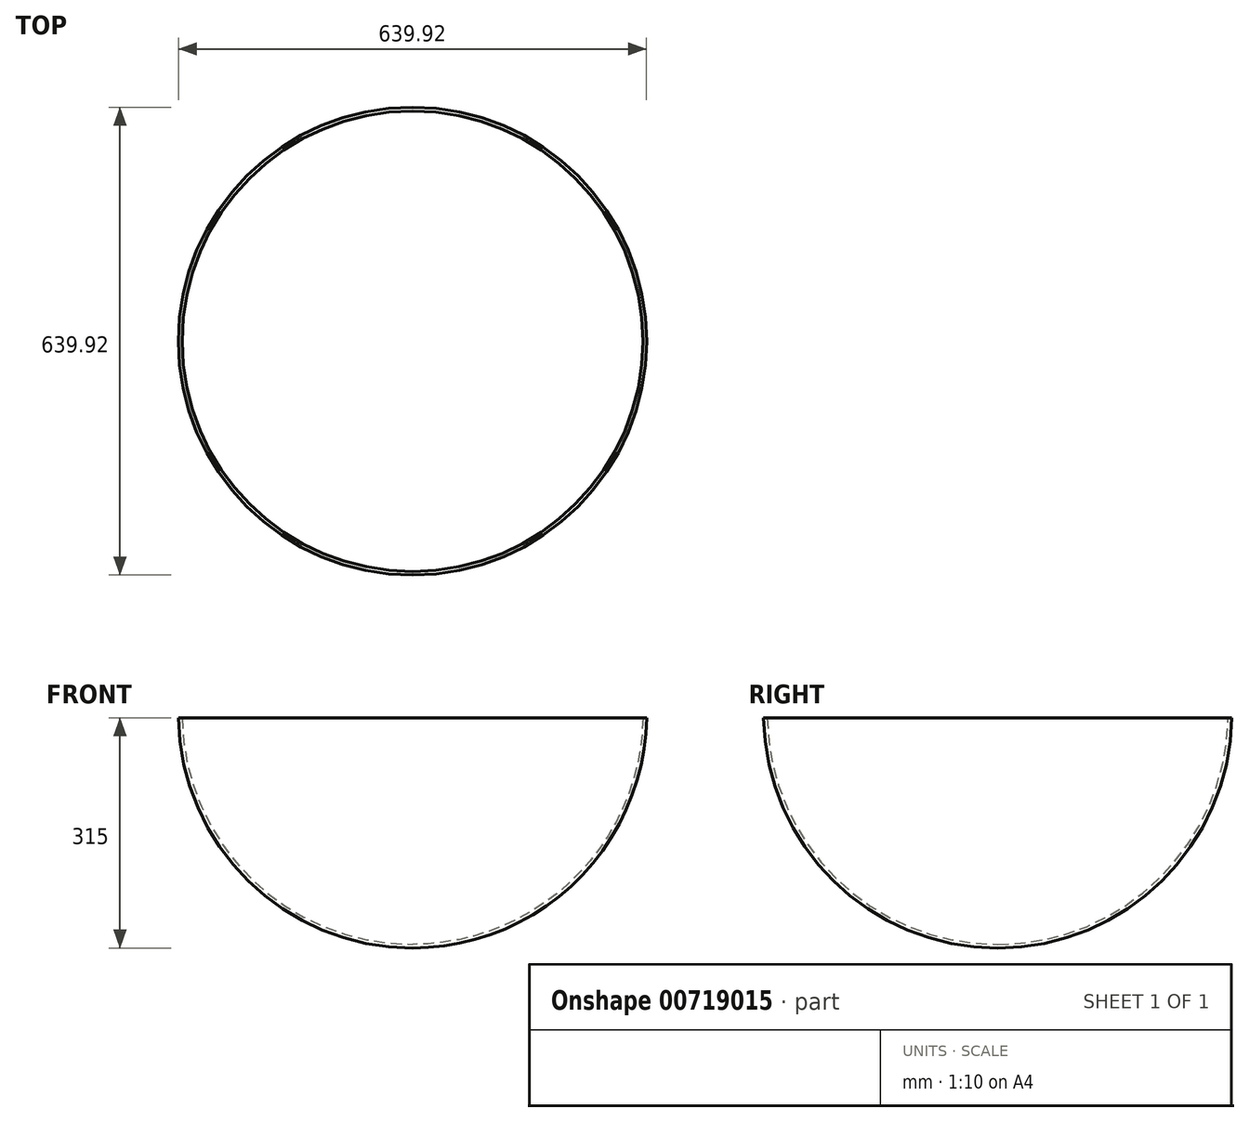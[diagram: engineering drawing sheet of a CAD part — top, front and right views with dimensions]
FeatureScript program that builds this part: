
annotation { "Feature Type Name" : "Feature", "Feature Type Description" : "" }
export const myFeature = defineFeature(function(context is Context, id is Id, definition is map)
    precondition{}
    {
        {
            var Q0;
            Q0=qCreatedBy(makeId("Front.planeOp"),FACE);
            var sketch = newSketch(context, id + "F0", { "sketchPlane" : qUnion([Q0])});
            skArc(sketch, "E0.0", {"start": v(-180.44, -139.56) * mm, "mid": v(44.06, -47.6) * mm, "end": v(139.52, 175.44) * mm});
            skArc(sketch, "E1.0", {"start": v(-180.44, -134.56) * mm, "mid": v(40.53, -44.06) * mm, "end": v(134.52, 175.44) * mm});
            skLineSegment(sketch, "E2", {"start": v(-180.44, -134.56) * mm, "end": v(-180.44, -139.56) * mm});
            skLineSegment(sketch, "E3", {"start": v(134.52, 175.44) * mm, "end": v(139.52, 175.44) * mm});
            skLineSegment(sketch, "E4", {"start": v(-180.44, -134.56) * mm, "end": v(-180.44, 180.44) * mm, "construction": true});
            skLineSegment(sketch, "E5", {"start": v(-180.44, 175.44) * mm, "end": v(189.02, 175.44) * mm, "construction": true});
            skSolve(sketch);
        }
        {
            var Q0;
            Q0 = qSketchRegion(id + "F0", true);
            var Q1;
            Q1=sQuery(id+"F0.wireOp",EDGE,"E4");
            revolve(context, id + "F1", {"surfaceOperationType" : NewSurfaceOperationType.NEW, "entities" : qUnion([Q0]), "axis" : qUnion([Q1]), "revolveType" : RevolveType.FULL});
        }
    });
